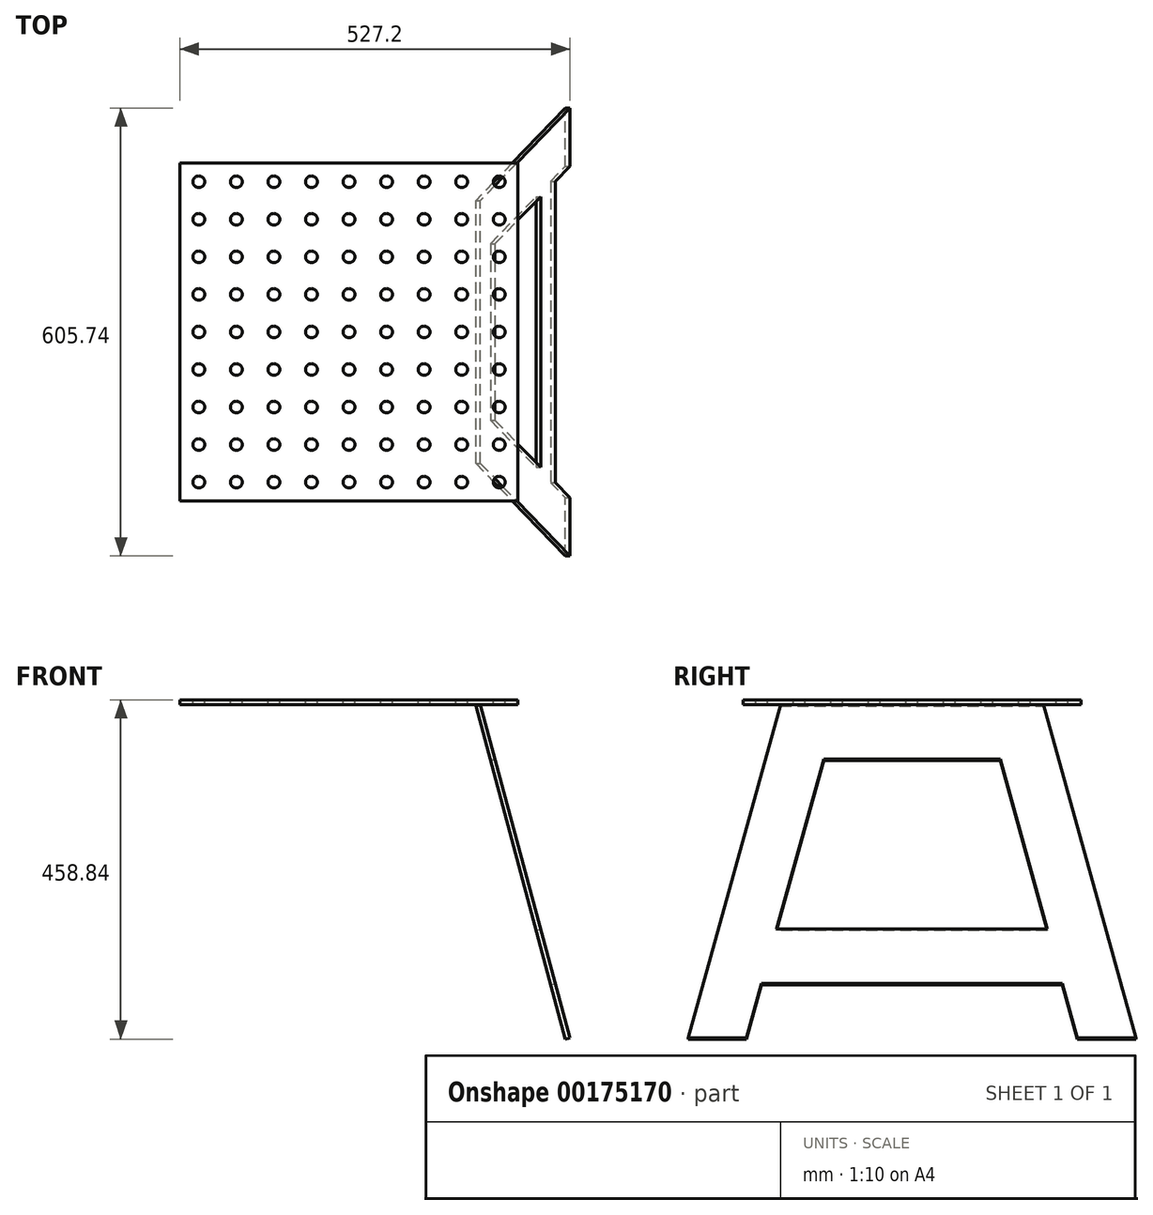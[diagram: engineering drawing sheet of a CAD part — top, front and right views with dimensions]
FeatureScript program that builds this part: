
annotation { "Feature Type Name" : "Feature", "Feature Type Description" : "" }
export const myFeature = defineFeature(function(context is Context, id is Id, definition is map)
    precondition{}
    {
        {
            var Q0;
            Q0=qCreatedBy(makeId("Top.planeOp"),FACE);
            var sketch = newSketch(context, id + "F0", { "sketchPlane" : qUnion([Q0])});
            skLineSegment(sketch, "E0.bottom", {"start": v(-228.6, 228.6) * mm, "end": v(228.6, 228.6) * mm});
            skLineSegment(sketch, "E0.top", {"start": v(-228.6, -228.6) * mm, "end": v(228.6, -228.6) * mm});
            skLineSegment(sketch, "E0.left", {"start": v(-228.6, 228.6) * mm, "end": v(-228.6, -228.6) * mm});
            skLineSegment(sketch, "E0.right", {"start": v(228.6, 228.6) * mm, "end": v(228.6, -228.6) * mm});
            skLineSegment(sketch, "E1", {"start": v(0, 0) * mm, "end": v(0, 419.07) * mm, "construction": true});
            skLineSegment(sketch, "E2", {"start": v(0, 0) * mm, "end": v(-437.99, 0) * mm, "construction": true});
            skPoint(sketch, "E3", {"position": v(0, 228.6) * mm});
            skPoint(sketch, "E4", {"position": v(-228.6, 0) * mm});
            skSolve(sketch);
        }
        {
            var Q0;
            Q0 = qSketchRegion(id + "F0", true);
            extrude(context, id + "F1", {"entities" : qUnion([Q0]), "depth" : 6.35 * mm});
        }
        {
            var Q0;
            Q0=makeQuery(id+"F1.opExtrude","CAP_FACE",FACE,{"disambiguationData":[OSD([sQuery(id+"F0.wireOp",EDGE,"E0.bottom"),sQuery(id+"F0.wireOp",EDGE,"E0.top"),sQuery(id+"F0.wireOp",EDGE,"E0.left"),sQuery(id+"F0.wireOp",EDGE,"E0.right")])],"isStart":false});
            var sketch = newSketch(context, id + "F2", { "sketchPlane" : qUnion([Q0])});
            skLineSegment(sketch, "E5", {"start": v(-338.38, 203.2) * mm, "end": v(337.4, 203.2) * mm, "construction": true});
            skLineSegment(sketch, "E6", {"start": v(-203.2, 252.84) * mm, "end": v(-203.2, -243.05) * mm, "construction": true});
            skCircle(sketch, "E7", {"center": v(-203.2, 203.2) * mm, "radius": 7.94 * mm});
            skCircle(sketch, "E8.0.1.0", {"center": v(-203.2, 152.4) * mm, "radius": 7.94 * mm});
            skCircle(sketch, "E8.0.2.0", {"center": v(-203.2, 101.6) * mm, "radius": 7.94 * mm});
            skCircle(sketch, "E8.0.3.0", {"center": v(-203.2, 50.8) * mm, "radius": 7.94 * mm});
            skCircle(sketch, "E8.0.4.0", {"center": v(-203.2, 0) * mm, "radius": 7.94 * mm});
            skCircle(sketch, "E8.0.5.0", {"center": v(-203.2, -50.8) * mm, "radius": 7.94 * mm});
            skCircle(sketch, "E8.0.6.0", {"center": v(-203.2, -101.6) * mm, "radius": 7.94 * mm});
            skCircle(sketch, "E8.0.7.0", {"center": v(-203.2, -152.4) * mm, "radius": 7.94 * mm});
            skCircle(sketch, "E8.0.8.0", {"center": v(-203.2, -203.2) * mm, "radius": 7.94 * mm});
            skCircle(sketch, "E8.1.0.0", {"center": v(-152.4, 203.2) * mm, "radius": 7.94 * mm});
            skCircle(sketch, "E8.1.1.0", {"center": v(-152.4, 152.4) * mm, "radius": 7.94 * mm});
            skCircle(sketch, "E8.1.2.0", {"center": v(-152.4, 101.6) * mm, "radius": 7.94 * mm});
            skCircle(sketch, "E8.1.3.0", {"center": v(-152.4, 50.8) * mm, "radius": 7.94 * mm});
            skCircle(sketch, "E8.1.4.0", {"center": v(-152.4, 0) * mm, "radius": 7.94 * mm});
            skCircle(sketch, "E8.1.5.0", {"center": v(-152.4, -50.8) * mm, "radius": 7.94 * mm});
            skCircle(sketch, "E8.1.6.0", {"center": v(-152.4, -101.6) * mm, "radius": 7.94 * mm});
            skCircle(sketch, "E8.1.7.0", {"center": v(-152.4, -152.4) * mm, "radius": 7.94 * mm});
            skCircle(sketch, "E8.1.8.0", {"center": v(-152.4, -203.2) * mm, "radius": 7.94 * mm});
            skCircle(sketch, "E8.2.0.0", {"center": v(-101.6, 203.2) * mm, "radius": 7.94 * mm});
            skCircle(sketch, "E8.2.1.0", {"center": v(-101.6, 152.4) * mm, "radius": 7.94 * mm});
            skCircle(sketch, "E8.2.2.0", {"center": v(-101.6, 101.6) * mm, "radius": 7.94 * mm});
            skCircle(sketch, "E8.2.3.0", {"center": v(-101.6, 50.8) * mm, "radius": 7.94 * mm});
            skCircle(sketch, "E8.2.4.0", {"center": v(-101.6, 0) * mm, "radius": 7.94 * mm});
            skCircle(sketch, "E8.2.5.0", {"center": v(-101.6, -50.8) * mm, "radius": 7.94 * mm});
            skCircle(sketch, "E8.2.6.0", {"center": v(-101.6, -101.6) * mm, "radius": 7.94 * mm});
            skCircle(sketch, "E8.2.7.0", {"center": v(-101.6, -152.4) * mm, "radius": 7.94 * mm});
            skCircle(sketch, "E8.2.8.0", {"center": v(-101.6, -203.2) * mm, "radius": 7.94 * mm});
            skCircle(sketch, "E8.3.0.0", {"center": v(-50.8, 203.2) * mm, "radius": 7.94 * mm});
            skCircle(sketch, "E8.3.1.0", {"center": v(-50.8, 152.4) * mm, "radius": 7.94 * mm});
            skCircle(sketch, "E8.3.2.0", {"center": v(-50.8, 101.6) * mm, "radius": 7.94 * mm});
            skCircle(sketch, "E8.3.3.0", {"center": v(-50.8, 50.8) * mm, "radius": 7.94 * mm});
            skCircle(sketch, "E8.3.4.0", {"center": v(-50.8, 0) * mm, "radius": 7.94 * mm});
            skCircle(sketch, "E8.3.5.0", {"center": v(-50.8, -50.8) * mm, "radius": 7.94 * mm});
            skCircle(sketch, "E8.3.6.0", {"center": v(-50.8, -101.6) * mm, "radius": 7.94 * mm});
            skCircle(sketch, "E8.3.7.0", {"center": v(-50.8, -152.4) * mm, "radius": 7.94 * mm});
            skCircle(sketch, "E8.3.8.0", {"center": v(-50.8, -203.2) * mm, "radius": 7.94 * mm});
            skCircle(sketch, "E8.4.0.0", {"center": v(0, 203.2) * mm, "radius": 7.94 * mm});
            skCircle(sketch, "E8.4.1.0", {"center": v(0, 152.4) * mm, "radius": 7.94 * mm});
            skCircle(sketch, "E8.4.2.0", {"center": v(0, 101.6) * mm, "radius": 7.94 * mm});
            skCircle(sketch, "E8.4.3.0", {"center": v(0, 50.8) * mm, "radius": 7.94 * mm});
            skCircle(sketch, "E8.4.4.0", {"center": v(0, 0) * mm, "radius": 7.94 * mm});
            skCircle(sketch, "E8.4.5.0", {"center": v(0, -50.8) * mm, "radius": 7.94 * mm});
            skCircle(sketch, "E8.4.6.0", {"center": v(0, -101.6) * mm, "radius": 7.94 * mm});
            skCircle(sketch, "E8.4.7.0", {"center": v(0, -152.4) * mm, "radius": 7.94 * mm});
            skCircle(sketch, "E8.4.8.0", {"center": v(0, -203.2) * mm, "radius": 7.94 * mm});
            skCircle(sketch, "E8.5.0.0", {"center": v(50.8, 203.2) * mm, "radius": 7.94 * mm});
            skCircle(sketch, "E8.5.1.0", {"center": v(50.8, 152.4) * mm, "radius": 7.94 * mm});
            skCircle(sketch, "E8.5.2.0", {"center": v(50.8, 101.6) * mm, "radius": 7.94 * mm});
            skCircle(sketch, "E8.5.3.0", {"center": v(50.8, 50.8) * mm, "radius": 7.94 * mm});
            skCircle(sketch, "E8.5.4.0", {"center": v(50.8, 0) * mm, "radius": 7.94 * mm});
            skCircle(sketch, "E8.5.5.0", {"center": v(50.8, -50.8) * mm, "radius": 7.94 * mm});
            skCircle(sketch, "E8.5.6.0", {"center": v(50.8, -101.6) * mm, "radius": 7.94 * mm});
            skCircle(sketch, "E8.5.7.0", {"center": v(50.8, -152.4) * mm, "radius": 7.94 * mm});
            skCircle(sketch, "E8.5.8.0", {"center": v(50.8, -203.2) * mm, "radius": 7.94 * mm});
            skCircle(sketch, "E8.6.0.0", {"center": v(101.6, 203.2) * mm, "radius": 7.94 * mm});
            skCircle(sketch, "E8.6.1.0", {"center": v(101.6, 152.4) * mm, "radius": 7.94 * mm});
            skCircle(sketch, "E8.6.2.0", {"center": v(101.6, 101.6) * mm, "radius": 7.94 * mm});
            skCircle(sketch, "E8.6.3.0", {"center": v(101.6, 50.8) * mm, "radius": 7.94 * mm});
            skCircle(sketch, "E8.6.4.0", {"center": v(101.6, 0) * mm, "radius": 7.94 * mm});
            skCircle(sketch, "E8.6.5.0", {"center": v(101.6, -50.8) * mm, "radius": 7.94 * mm});
            skCircle(sketch, "E8.6.6.0", {"center": v(101.6, -101.6) * mm, "radius": 7.94 * mm});
            skCircle(sketch, "E8.6.7.0", {"center": v(101.6, -152.4) * mm, "radius": 7.94 * mm});
            skCircle(sketch, "E8.6.8.0", {"center": v(101.6, -203.2) * mm, "radius": 7.94 * mm});
            skCircle(sketch, "E8.7.0.0", {"center": v(152.4, 203.2) * mm, "radius": 7.94 * mm});
            skCircle(sketch, "E8.7.1.0", {"center": v(152.4, 152.4) * mm, "radius": 7.94 * mm});
            skCircle(sketch, "E8.7.2.0", {"center": v(152.4, 101.6) * mm, "radius": 7.94 * mm});
            skCircle(sketch, "E8.7.3.0", {"center": v(152.4, 50.8) * mm, "radius": 7.94 * mm});
            skCircle(sketch, "E8.7.4.0", {"center": v(152.4, 0) * mm, "radius": 7.94 * mm});
            skCircle(sketch, "E8.7.5.0", {"center": v(152.4, -50.8) * mm, "radius": 7.94 * mm});
            skCircle(sketch, "E8.7.6.0", {"center": v(152.4, -101.6) * mm, "radius": 7.94 * mm});
            skCircle(sketch, "E8.7.7.0", {"center": v(152.4, -152.4) * mm, "radius": 7.94 * mm});
            skCircle(sketch, "E8.7.8.0", {"center": v(152.4, -203.2) * mm, "radius": 7.94 * mm});
            skCircle(sketch, "E8.8.0.0", {"center": v(203.2, 203.2) * mm, "radius": 7.94 * mm});
            skCircle(sketch, "E8.8.1.0", {"center": v(203.2, 152.4) * mm, "radius": 7.94 * mm});
            skCircle(sketch, "E8.8.2.0", {"center": v(203.2, 101.6) * mm, "radius": 7.94 * mm});
            skCircle(sketch, "E8.8.3.0", {"center": v(203.2, 50.8) * mm, "radius": 7.94 * mm});
            skCircle(sketch, "E8.8.4.0", {"center": v(203.2, 0) * mm, "radius": 7.94 * mm});
            skCircle(sketch, "E8.8.5.0", {"center": v(203.2, -50.8) * mm, "radius": 7.94 * mm});
            skCircle(sketch, "E8.8.6.0", {"center": v(203.2, -101.6) * mm, "radius": 7.94 * mm});
            skCircle(sketch, "E8.8.7.0", {"center": v(203.2, -152.4) * mm, "radius": 7.94 * mm});
            skCircle(sketch, "E8.8.8.0", {"center": v(203.2, -203.2) * mm, "radius": 7.94 * mm});
            skLineSegment(sketch, "E8.direction1", {"start": v(-203.2, 203.2) * mm, "end": v(-152.4, 203.2) * mm, "construction": true});
            skLineSegment(sketch, "E8.direction2", {"start": v(-203.2, 203.2) * mm, "end": v(-203.2, 152.4) * mm, "construction": true});
            skSolve(sketch);
        }
        {
            var Q0;
            Q0 = qSketchRegion(id + "F2", true);
            extrude(context, id + "F3", {"entities" : qUnion([Q0]), "operationType" : NewBodyOperationType.REMOVE, "endBound" : BoundingType.UP_TO_NEXT, "oppositeDirection" : true, "depth" : 25.4 * mm});
        }
        {
            var Q0;
            Q0=makeQuery(id+"F1.opExtrude","CAP_FACE",FACE,{"disambiguationData":[OSD([sQuery(id+"F0.wireOp",EDGE,"E0.bottom"),sQuery(id+"F0.wireOp",EDGE,"E0.top"),sQuery(id+"F0.wireOp",EDGE,"E0.left"),sQuery(id+"F0.wireOp",EDGE,"E0.right")])],"isStart":true});
            var sketch = newSketch(context, id + "F4", { "sketchPlane" : qUnion([Q0])});
            skLineSegment(sketch, "E9.bottom", {"start": v(-177.8, 177.8) * mm, "end": v(177.8, 177.8) * mm});
            skLineSegment(sketch, "E9.top", {"start": v(-177.8, -177.8) * mm, "end": v(177.8, -177.8) * mm});
            skLineSegment(sketch, "E9.left", {"start": v(-177.8, 177.8) * mm, "end": v(-177.8, -177.8) * mm});
            skLineSegment(sketch, "E9.right", {"start": v(177.8, 177.8) * mm, "end": v(177.8, -177.8) * mm});
            skSolve(sketch);
        }
        {
            var Q0;
            Q0=sQuery(id+"F4.wireOp",EDGE,"E9.bottom");
            cPlane(context, id + "F5", {"entities" : qUnion([Q0]), "cplaneType" : CPlaneType.LINE_ANGLE, "offset" : 25.4 * mm, "angle" : 0 * degree, "width" : 152.4 * mm, "height" : 152.4 * mm});
        }
        {
            var Q0;
            Q0=qCreatedBy(id+"F5.planeOp",FACE);
            var sketch = newSketch(context, id + "F6", { "sketchPlane" : qUnion([Q0])});
            skPoint(sketch, "E10.0", {"position": v(-177.8, 0) * mm});
            skPoint(sketch, "E11.0", {"position": v(177.8, 0) * mm});
            skLineSegment(sketch, "E12.0", {"start": v(177.8, 0) * mm, "end": v(-177.8, 0) * mm});
            skLineSegment(sketch, "E13", {"start": v(-177.8, 0) * mm, "end": v(-298.6, -450.85) * mm});
            skLineSegment(sketch, "E14", {"start": v(-298.6, -450.85) * mm, "end": v(298.6, -450.85) * mm});
            skLineSegment(sketch, "E15", {"start": v(298.6, -450.85) * mm, "end": v(177.8, 0) * mm});
            skSolve(sketch);
        }
        {
            var Q0;
            Q0=sQuery(id+"F6.wireOp",EDGE,"E13");
            var Q1;
            Q1=makeQuery(id+"F1.opExtrude","CAP_EDGE",EDGE,{"disambiguationData":[OSD([sQuery(id+"F0.wireOp",EDGE,"E0.right")])],"isStart":true});
            cPlane(context, id + "F7", {"entities" : qUnion([Q0, Q1]), "cplaneType" : CPlaneType.LINE_ANGLE, "offset" : 25.4 * mm, "angle" : 0 * degree, "width" : 152.4 * mm, "height" : 152.4 * mm});
        }
        {
            var Q0;
            Q0=qCreatedBy(id+"F7.planeOp",FACE);
            var sketch = newSketch(context, id + "F8", { "sketchPlane" : qUnion([Q0])});
            skPoint(sketch, "E16.0", {"position": v(177.8, -46.02) * mm});
            skLineSegment(sketch, "E17.0", {"start": v(177.8, -46.02) * mm, "end": v(-177.8, -46.02) * mm});
            skPoint(sketch, "E18.0", {"position": v(177.8, -512.77) * mm});
            skLineSegment(sketch, "E19", {"start": v(177.8, -46.02) * mm, "end": v(302.87, -512.77) * mm});
            skLineSegment(sketch, "E20", {"start": v(302.87, -512.77) * mm, "end": v(-302.87, -512.77) * mm});
            skLineSegment(sketch, "E21", {"start": v(-302.87, -512.77) * mm, "end": v(-177.8, -46.02) * mm});
            skSolve(sketch);
        }
        {
            var Q0;
            Q0=makeQuery(id+"F8.imprint","IMPRINT",FACE,{"disambiguationData":[TD([[makeQuery(id+"F8.imprint","IMPRINT",EDGE,{"derivedFrom":sQuery(id+"F8.wireOp",EDGE,"E17.0")}),1.0]])]});
            extrude(context, id + "F9", {"entities" : qUnion([Q0]), "depth" : 6.35 * mm});
        }
        {
            var Q0;
            Q0=makeQuery(id+"F8.imprint","IMPRINT",FACE,{"disambiguationData":[TD([[makeQuery(id+"F8.imprint","IMPRINT",EDGE,{"derivedFrom":sQuery(id+"F8.wireOp",EDGE,"E17.0")}),1.0]])]});
            var sketch = newSketch(context, id + "F10", { "sketchPlane" : qUnion([Q0])});
            skLineSegment(sketch, "E22", {"start": v(-203.56, -436.57) * mm, "end": v(203.56, -436.57) * mm});
            skLineSegment(sketch, "E23", {"start": v(119.33, -122.22) * mm, "end": v(183.14, -360.37) * mm});
            skLineSegment(sketch, "E24", {"start": v(-119.33, -122.22) * mm, "end": v(-183.14, -360.37) * mm});
            skLineSegment(sketch, "E25", {"start": v(-119.33, -122.22) * mm, "end": v(119.33, -122.22) * mm});
            skLineSegment(sketch, "E26", {"start": v(-183.14, -360.37) * mm, "end": v(183.14, -360.37) * mm});
            skLineSegment(sketch, "E27.trimOffspring", {"start": v(203.56, -436.57) * mm, "end": v(223.98, -512.77) * mm});
            skLineSegment(sketch, "E28.trimOffspring", {"start": v(-203.56, -436.57) * mm, "end": v(-223.98, -512.77) * mm});
            skLineSegment(sketch, "E29", {"start": v(223.98, -512.77) * mm, "end": v(-223.98, -512.77) * mm});
            skSolve(sketch);
        }
        {
            var Q0;
            Q0=makeQuery(id+"F10.imprint","IMPRINT",FACE,{"disambiguationData":[TD([[makeQuery(id+"F10.imprint","IMPRINT",EDGE,{"derivedFrom":sQuery(id+"F10.wireOp",EDGE,"E23")}),-1.0]])]});
            var Q1;
            Q1=makeQuery(id+"F10.imprint","IMPRINT",FACE,{"disambiguationData":[TD([[makeQuery(id+"F10.imprint","IMPRINT",EDGE,{"derivedFrom":sQuery(id+"F10.wireOp",EDGE,"E22")}),-1.0]])]});
            var Q2;
            Q2=sQuery(id+"F10.wireOp",EDGE,"E23");
            var Q3;
            Q3=sQuery(id+"F10.wireOp",EDGE,"E25");
            var Q4;
            Q4=sQuery(id+"F10.wireOp",EDGE,"E24");
            var Q5;
            Q5=sQuery(id+"F10.wireOp",EDGE,"E26");
            extrude(context, id + "F11", {"entities" : qUnion([Q0, Q1]), "operationType" : NewBodyOperationType.REMOVE, "surfaceEntities" : qUnion([Q2, Q3, Q4, Q5]), "endBound" : BoundingType.UP_TO_NEXT, "depth" : 25.4 * mm});
        }
    });
